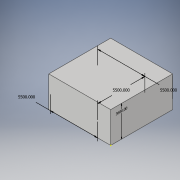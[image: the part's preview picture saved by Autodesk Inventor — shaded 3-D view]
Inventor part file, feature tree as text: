
AUTODESK INVENTOR PART (.ipt)
format: ipt  version: 2018 (Build 220112000, 112)  size: 109,056 bytes
history: native  units: in
note: dims shown in document units (in); Inventor stores cm internally (conversion verified against a paired STEP export)
features: other x3, sketch x3, extrude x1
ambient origin geometry x8: Origin, YZ Plane, XZ Plane, XY Plane, X Axis, Y Axis, Z Axis, Center Point
bodies: Solid1 (feature_tree)
feature tree (7):
  other  "Annotations"
  sketch  "Sketch1"  dims[d0=7200.0in d1=7200.0in]
  extrude  "Extrusion1"  Depth=7200.0in
  sketch  "3D Sketch17"
  sketch  "Sketch2"  dims[d2=3600.0in d3=0.0in d29=5500.0in d30=5500.0in d31=5500.0in d22=0.1318in d23=3600.0in d24=7200.0in]
  other  "Linear Dimension 1"
  other  "Linear Dimension 2"
